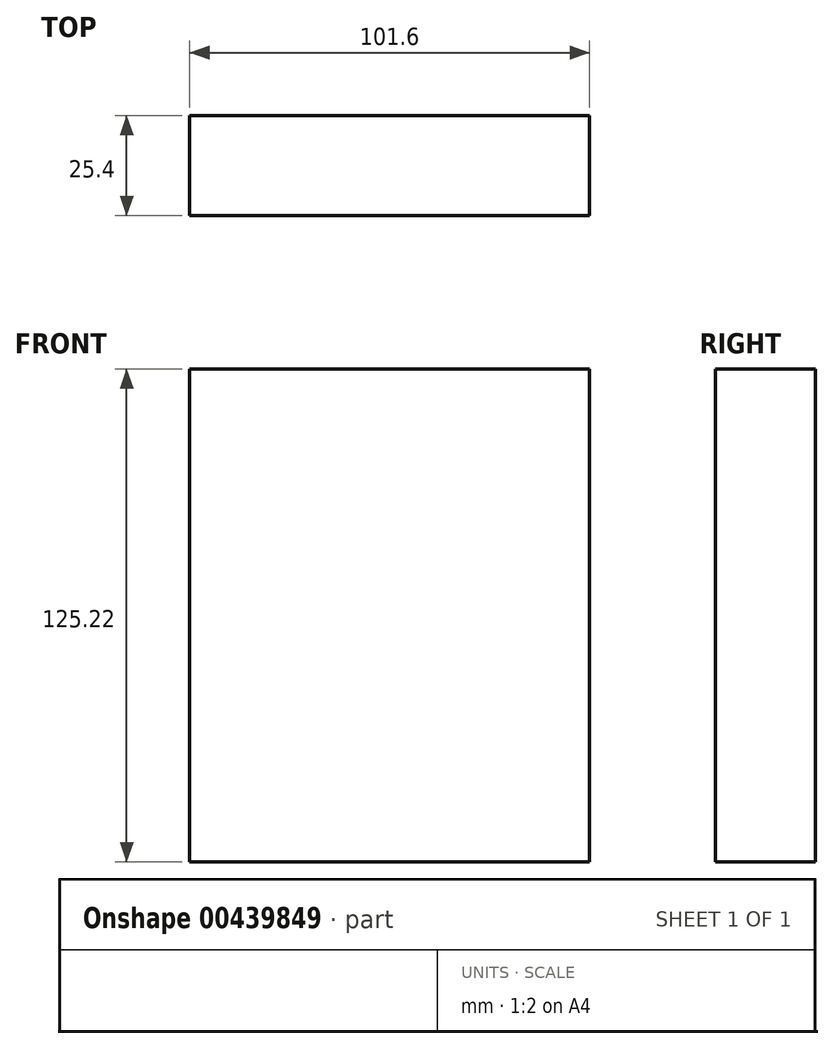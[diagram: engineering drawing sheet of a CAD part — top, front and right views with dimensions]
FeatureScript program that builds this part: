
annotation { "Feature Type Name" : "Feature", "Feature Type Description" : "" }
export const myFeature = defineFeature(function(context is Context, id is Id, definition is map)
    precondition{}
    {
        {
            var Q0;
            Q0=qCreatedBy(makeId("Front.planeOp"),FACE);
            var sketch = newSketch(context, id + "F0", { "sketchPlane" : qUnion([Q0])});
            skLineSegment(sketch, "E0", {"start": v(50.8, 62.61) * mm, "end": v(50.8, -62.61) * mm});
            skLineSegment(sketch, "E1", {"start": v(50.8, -62.61) * mm, "end": v(-50.8, -62.61) * mm});
            skLineSegment(sketch, "E2", {"start": v(-50.8, -62.61) * mm, "end": v(-50.8, 62.61) * mm});
            skLineSegment(sketch, "E3", {"start": v(-50.8, 62.61) * mm, "end": v(50.8, 62.61) * mm});
            skSolve(sketch);
        }
        {
            var Q0;
            Q0=makeQuery(id+"F0.imprint","IMPRINT",FACE,{"disambiguationData":[TD([[makeQuery(id+"F0.imprint","IMPRINT",EDGE,{"derivedFrom":sQuery(id+"F0.wireOp",EDGE,"E0")}),-1.0]])]});
            extrude(context, id + "F1", {"entities" : qUnion([Q0]), "depth" : 25.4 * mm});
        }
    });
